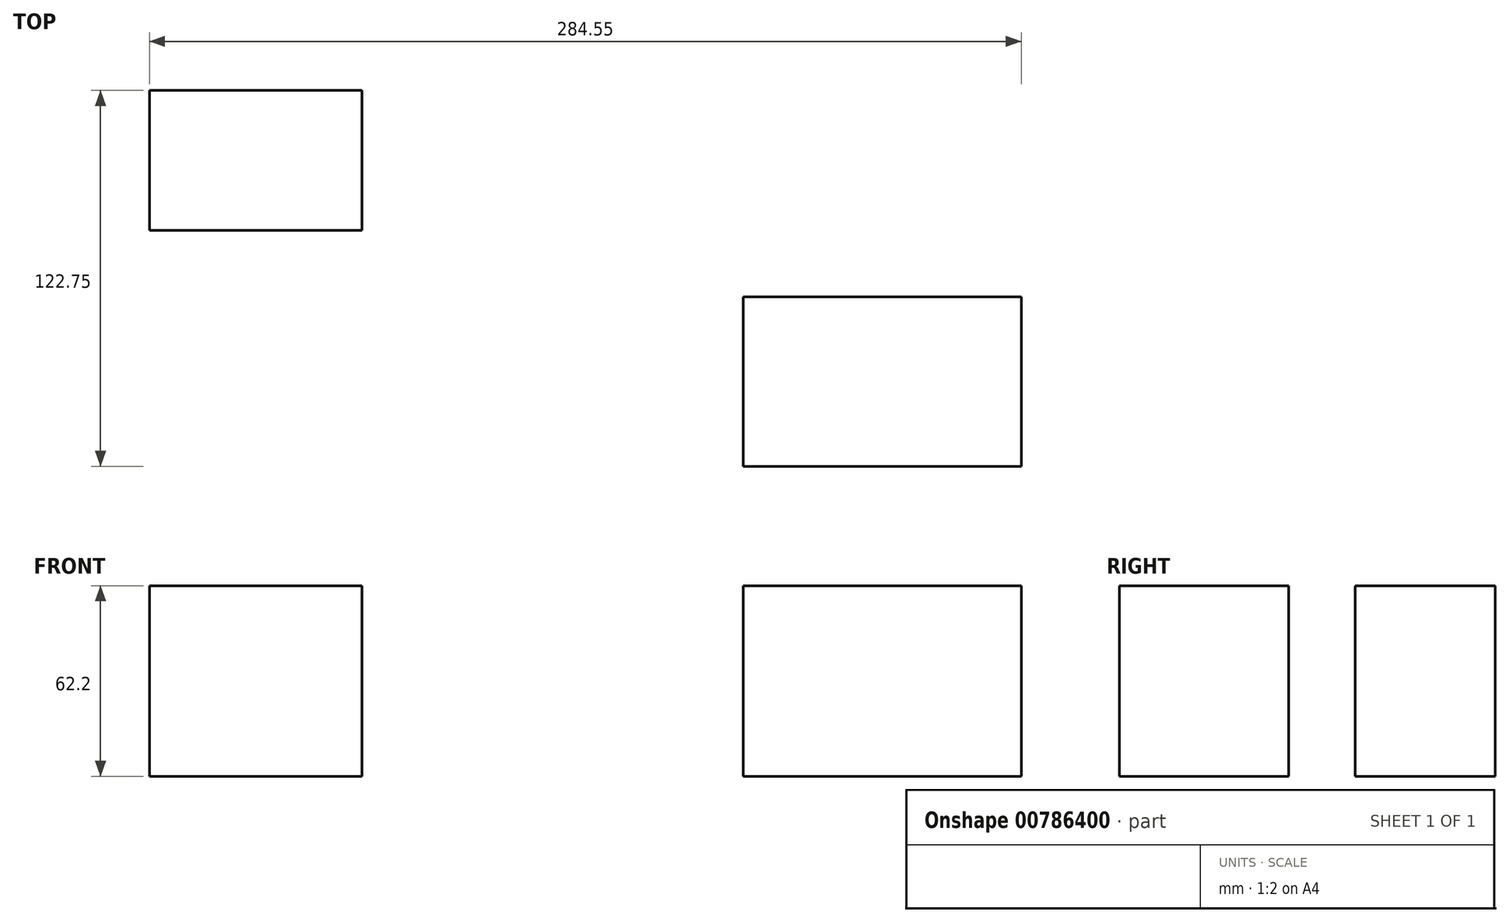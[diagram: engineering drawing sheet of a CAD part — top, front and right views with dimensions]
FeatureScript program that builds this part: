
annotation { "Feature Type Name" : "Feature", "Feature Type Description" : "" }
export const myFeature = defineFeature(function(context is Context, id is Id, definition is map)
    precondition{}
    {
        {
            var Q0;
            Q0=qCreatedBy(makeId("Top.planeOp"),FACE);
            var sketch = newSketch(context, id + "F0", { "sketchPlane" : qUnion([Q0])});
            skLineSegment(sketch, "E0.bottom", {"start": v(-173.65, 45.74) * mm, "end": v(-104.31, 45.74) * mm});
            skLineSegment(sketch, "E0.top", {"start": v(-173.65, 0) * mm, "end": v(-104.31, 0) * mm});
            skLineSegment(sketch, "E0.left", {"start": v(-173.65, 45.74) * mm, "end": v(-173.65, 0) * mm});
            skLineSegment(sketch, "E0.right", {"start": v(-104.31, 45.74) * mm, "end": v(-104.31, 0) * mm});
            skLineSegment(sketch, "E1.bottom", {"start": v(20.14, -21.68) * mm, "end": v(110.9, -21.68) * mm});
            skLineSegment(sketch, "E1.top", {"start": v(20.14, -77) * mm, "end": v(110.9, -77) * mm});
            skLineSegment(sketch, "E1.left", {"start": v(20.14, -21.68) * mm, "end": v(20.14, -77) * mm});
            skLineSegment(sketch, "E1.right", {"start": v(110.9, -21.68) * mm, "end": v(110.9, -77) * mm});
            skSolve(sketch);
        }
        {
            var Q0;
            Q0 = qSketchRegion(id + "F0", true);
            extrude(context, id + "F1", {"entities" : qUnion([Q0]), "depth" : 62.2 * mm, "offsetDistance" : 25 * mm});
        }
    });
